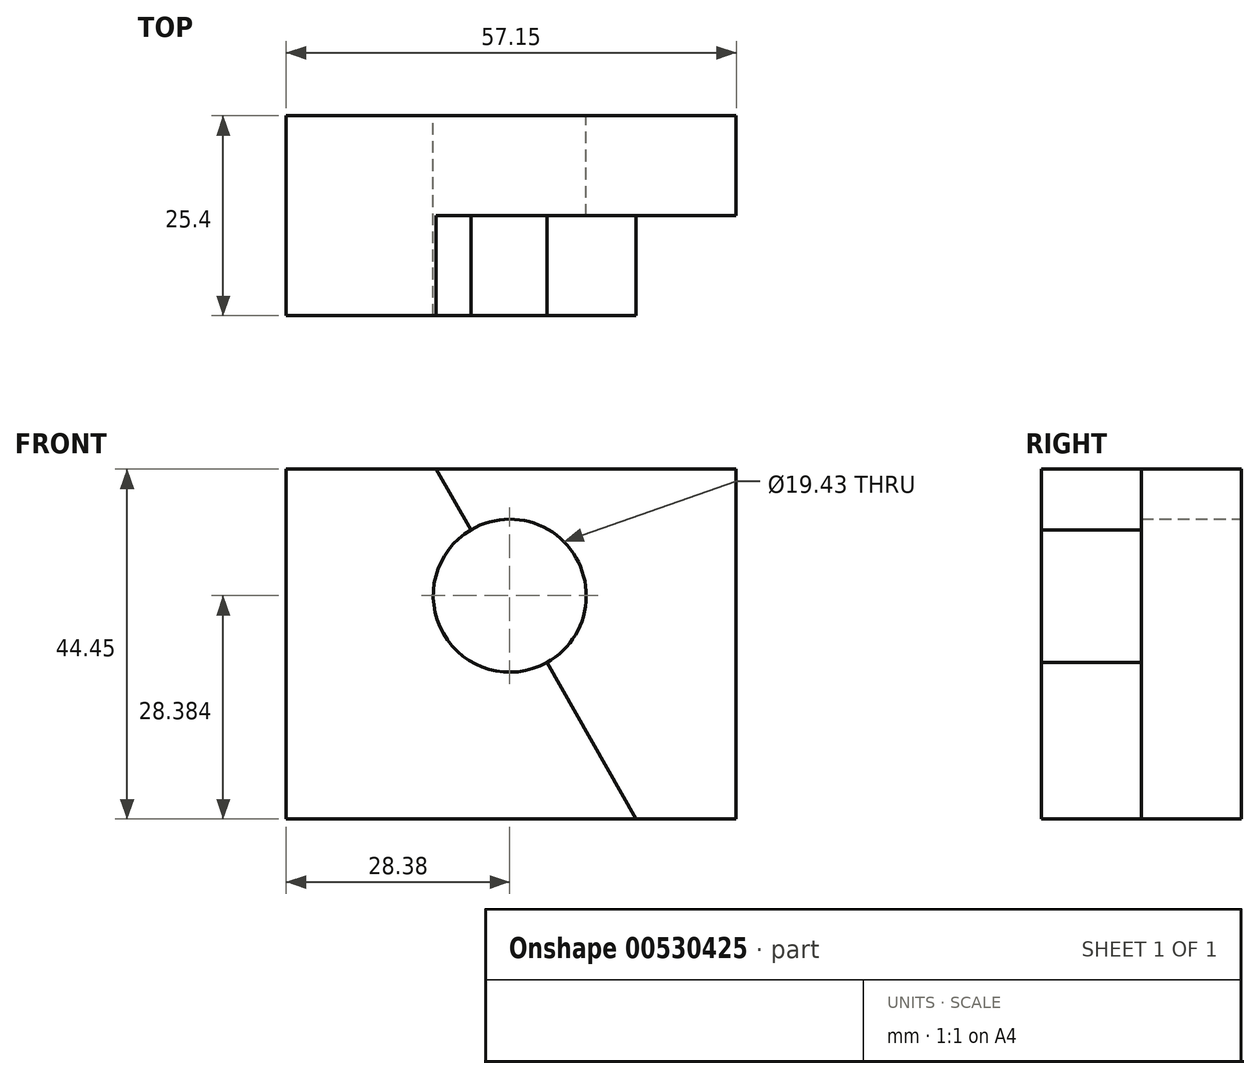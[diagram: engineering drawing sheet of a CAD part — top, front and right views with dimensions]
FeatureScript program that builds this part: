
annotation { "Feature Type Name" : "Feature", "Feature Type Description" : "" }
export const myFeature = defineFeature(function(context is Context, id is Id, definition is map)
    precondition{}
    {
        {
            var Q0;
            Q0=qCreatedBy(makeId("Front.planeOp"),FACE);
            var sketch = newSketch(context, id + "F0", { "sketchPlane" : qUnion([Q0])});
            skLineSegment(sketch, "E0.bottom", {"start": v(-28.38, 44.45) * mm, "end": v(28.77, 44.45) * mm});
            skLineSegment(sketch, "E0.top", {"start": v(-28.38, 0) * mm, "end": v(28.77, 0) * mm});
            skLineSegment(sketch, "E0.left", {"start": v(-28.38, 44.45) * mm, "end": v(-28.38, 0) * mm});
            skLineSegment(sketch, "E0.right", {"start": v(28.77, 44.45) * mm, "end": v(28.77, 0) * mm});
            skSolve(sketch);
        }
        {
            var Q0;
            Q0=makeQuery(id+"F0.imprint","IMPRINT",FACE,{"disambiguationData":[TD([[makeQuery(id+"F0.imprint","IMPRINT",EDGE,{"derivedFrom":sQuery(id+"F0.wireOp",EDGE,"E0.bottom")}),-1.0]])]});
            extrude(context, id + "F1", {"entities" : qUnion([Q0]), "depth" : 25.4 * mm, "offsetDistance" : 25.4 * mm});
        }
        {
            var Q0;
            Q0=makeQuery(id+"F1.opExtrude","SWEPT_FACE",FACE,{"disambiguationData":[OSD([sQuery(id+"F0.wireOp",EDGE,"E0.bottom")])]});
            var sketch = newSketch(context, id + "F2", { "sketchPlane" : qUnion([Q0])});
            skLineSegment(sketch, "E1.bottom", {"start": v(28.77, -25.4) * mm, "end": v(-9.33, -25.4) * mm});
            skLineSegment(sketch, "E1.top", {"start": v(28.77, -12.7) * mm, "end": v(-9.33, -12.7) * mm});
            skLineSegment(sketch, "E1.left", {"start": v(28.77, -25.4) * mm, "end": v(28.77, -12.7) * mm});
            skLineSegment(sketch, "E1.right", {"start": v(-9.33, -25.4) * mm, "end": v(-9.33, -12.7) * mm});
            skSolve(sketch);
        }
        {
            var Q0;
            Q0=makeQuery(id+"F2.imprint","IMPRINT",FACE,{"disambiguationData":[TD([[makeQuery(id+"F2.imprint","IMPRINT",EDGE,{"derivedFrom":sQuery(id+"F2.wireOp",EDGE,"E1.bottom")}),1.0]])]});
            extrude(context, id + "F3", {"entities" : qUnion([Q0]), "operationType" : NewBodyOperationType.REMOVE, "oppositeDirection" : true, "depth" : 44.45 * mm, "offsetDistance" : 25.4 * mm});
        }
        {
            var Q0;
            Q0=makeQuery(id+"F3.boolean.opBoolean","COPY",FACE,{"derivedFrom":makeQuery(id+"F3.opExtrude","SWEPT_FACE",FACE,{"disambiguationData":[OSD([sQuery(id+"F2.wireOp",EDGE,"E1.top")])]})});
            var sketch = newSketch(context, id + "F4", { "sketchPlane" : qUnion([Q0])});
            skLineSegment(sketch, "E2", {"start": v(-9.33, 44.45) * mm, "end": v(16.07, 0) * mm});
            skSolve(sketch);
        }
        {
            var Q0;
            {var subQ0=sQuery(id+"F4.wireOp",EDGE,"E2");Q0=makeQuery(id+"F4.imprint","IMPRINT",FACE,{"disambiguationData":[TD([[makeQuery(id+"F4.imprint","IMPRINT",EDGE,{"derivedFrom":subQ0}),-1.0]])]});}
            extrude(context, id + "F5", {"entities" : qUnion([Q0]), "operationType" : NewBodyOperationType.ADD, "depth" : 12.7 * mm, "offsetDistance" : 25.4 * mm});
        }
        {
            var Q0;
            Q0=qCreatedBy(makeId("Front.planeOp"),FACE);
            var sketch = newSketch(context, id + "F6", { "sketchPlane" : qUnion([Q0])});
            skCircle(sketch, "E3", {"center": v(0, 28.38) * mm, "radius": 9.72 * mm});
            skSolve(sketch);
        }
        {
            var Q0;
            Q0=makeQuery(id+"F6.imprint","IMPRINT",FACE,{"disambiguationData":[TD([[makeQuery(id+"F6.imprint","IMPRINT",EDGE,{"derivedFrom":sQuery(id+"F6.wireOp",EDGE,"E3")}),1.0]])]});
            extrude(context, id + "F7", {"entities" : qUnion([Q0]), "operationType" : NewBodyOperationType.REMOVE, "endBound" : BoundingType.THROUGH_ALL, "depth" : 25.4 * mm, "offsetDistance" : 25.4 * mm});
        }
    });
